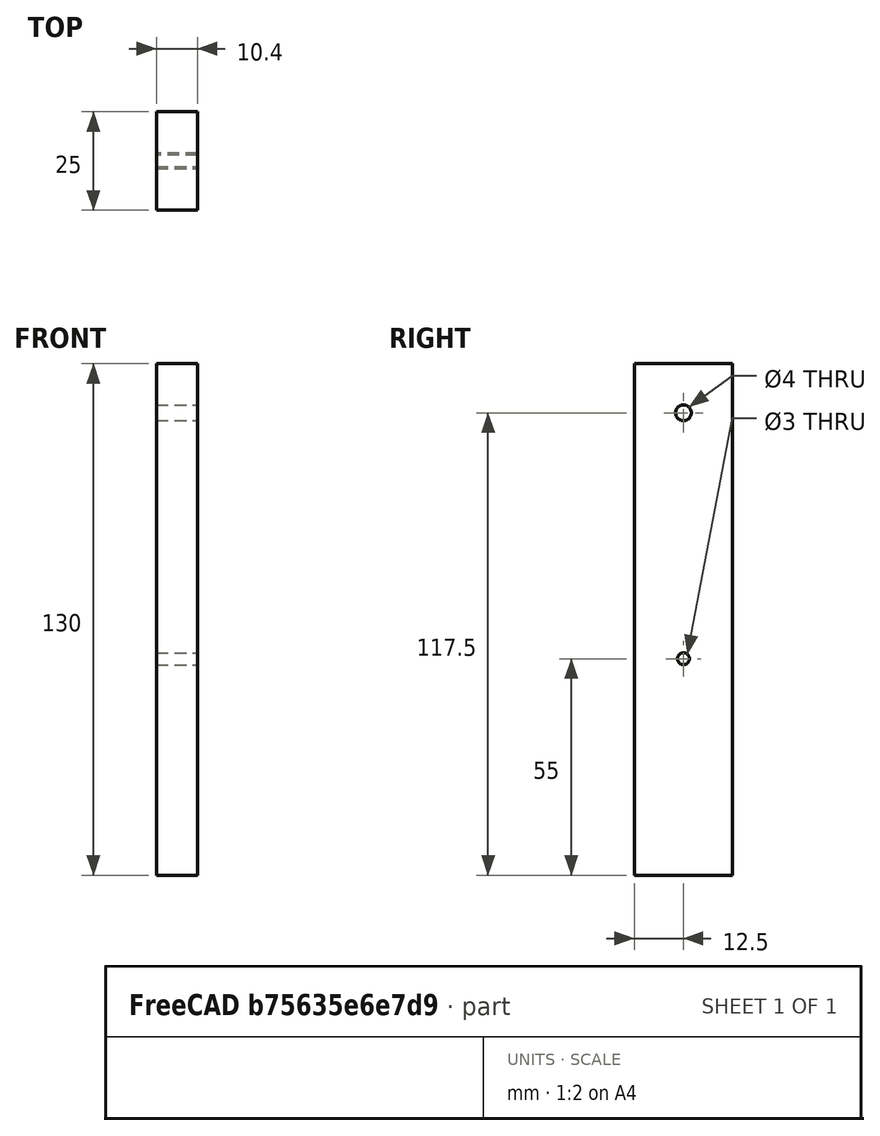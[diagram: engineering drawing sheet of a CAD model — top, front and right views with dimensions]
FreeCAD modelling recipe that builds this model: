
FCSTD DOCUMENT  (FreeCAD 0.19R24267 +99 (Git))
Label: Standbeine
License: All rights reserved
LicenseURL: http://en.wikipedia.org/wiki/All_rights_reserved
objects: TechDraw::DrawViewDimension×6, TechDraw::DrawProjGroupItem×4, TechDraw::DrawProjGroup×4, Sketcher::SketchObject×3, PartDesign::Pocket×2, PartDesign::Pad×1, PartDesign::Body×1, TechDraw::DrawSVGTemplate×1, TechDraw::DrawPage×1
note: 10 computed .brp shape members not serialized (recipe doc carries the construction recipe); baked Part::Feature solids carry a one-line shape summary decoded from their .brp

FEATURE [Sketcher::SketchObject] Sketch
  FullyConstrained = true
  MapMode = 5
  Support = -> [XY_Plane]
  sketch-geometry (4):
    g0: LineSegment StartX=-5.2 StartY=12.5 StartZ=0 EndX=5.2 EndY=12.5 EndZ=0
    g1: LineSegment StartX=5.2 StartY=12.5 StartZ=0 EndX=5.2 EndY=-12.5 EndZ=0
    g2: LineSegment StartX=5.2 StartY=-12.5 StartZ=0 EndX=-5.2 EndY=-12.5 EndZ=0
    g3: LineSegment StartX=-5.2 StartY=-12.5 StartZ=0 EndX=-5.2 EndY=12.5 EndZ=0
  constraints (11):
    c: Coincident(g0,g1)
    c: Coincident(g1,g2)
    c: Coincident(g2,g3)
    c: Coincident(g3,g0)
    c: Horizontal(g0)
    c: Horizontal(g2)
    c: Vertical(g1)
    c: Vertical(g3)
    c: DistanceY(g1,g1) = 25
    c: DistanceX(g0,g0) = 10.4
    c: Symmetric(g0,g1,g-1)
FEATURE [PartDesign::Pad] Pad
  Direction = (1,1,1)
  Length = 130
  Length2 = 100
  Profile = -> Sketch
  Type = 0
FEATURE [Sketcher::SketchObject] Sketch001
  FullyConstrained = true
  MapMode = 5
  Placement = pos=(5.2,0,0) rot=(0.57735,0.57735,0.57735;2.0944rad)
  Support = -> [Pad]
  sketch-geometry (2):
    g0: Circle CenterX=0 CenterY=55 CenterZ=0 NormalX=0 NormalY=0 NormalZ=1 AngleXU=0 Radius=1.5
    g1: GeomPoint X=0 Y=53.5 Z=0
  constraints (6):
    c: PointOnObject(g0,g-2)
    c: DistanceY(g-1,g0) = 55
    c: Diameter(g0) = 3
    c: PointOnObject(g1,g0)
    c: PointOnObject(g1,g-2)
    c: DistanceY(g-1,g1) = 53.5
FEATURE [PartDesign::Pocket] Pocket
  BaseFeature = -> Pad
  Length = 100
  Length2 = 100
  Profile = -> Sketch001
  Type = 0
FEATURE [Sketcher::SketchObject] Sketch002
  ExternalGeometry = -> [Pocket]
  FullyConstrained = true
  MapMode = 5
  Placement = pos=(5.2,0,0) rot=(0.57735,0.57735,0.57735;2.0944rad)
  Support = -> [Pocket]
  sketch-geometry (3):
    g0: Circle CenterX=0 CenterY=117.5 CenterZ=0 NormalX=0 NormalY=0 NormalZ=1 AngleXU=0 Radius=2
    g1: LineSegment StartX=12.5 StartY=130 StartZ=0 EndX=0 EndY=130 EndZ=0
    g2: LineSegment StartX=0 StartY=130 StartZ=0 EndX=0 EndY=117.5 EndZ=0
  constraints (8):
    c: PointOnObject(g0,g-2)
    c: Coincident(g1,g-3)
    c: PointOnObject(g1,g-2)
    c: Horizontal(g1)
    c: Coincident(g2,g1)
    c: Coincident(g2,g0)
    c: Equal(g2,g1)
    c: Diameter(g0) = 4
FEATURE [PartDesign::Pocket] Pocket001
  BaseFeature = -> Pocket
  Length = 100
  Length2 = 100
  Profile = -> Sketch002
  Type = 0
FEATURE [PartDesign::Body] Body
  Group = -> [Sketch,Pad,Sketch001,Pocket,Sketch002,Pocket001]
  Origin = -> Origin
  Tip = -> Pocket001
FEATURE [TechDraw::DrawSVGTemplate] Template
  EditableTexts = APPROVER_NAME=APPROVER NAME; AUTHOR_NAME=AUTHOR NAME; DATE=YYYY-MM-DD; DN=DN; DOCUMENT_TYPE=Mechanical assembly drawing; OWNER_NAME=OWNER NAME; PM=PM; PN=PN; REVISION=REV A; RIGHTS=(R) DO NOT DUPLICATE THIS DRAWING TO THIRD PARTIES WITHOUT OWNER'S PERMISSION !; SCALE=M x:x; SHEET=99 of 99; SIZE=A4; TITLELINE-1=FreeCAD; TOLERANCE=+/- ?
  Height = 210
  Orientation = 1
  Width = 297
FEATURE [TechDraw::DrawProjGroupItem] ProjItem  label="Front"
  Caption = Seitenansicht
  CoarseView = false
  Direction = (1,0,0)
  Focus = 100
  HardHidden = false
  IsoCount = 0
  IsoHidden = false
  IsoVisible = false
  LockPosition = true
  Perspective = false
  Rotation = 0
  RotationVector = (0,1,0)
  ScaleType = 2
  SeamHidden = false
  SeamVisible = true
  SmoothHidden = false
  SmoothVisible = true
  Source = -> [Body]
  Type = 0
  X = 0
  XDirection = (0,1,0)
  Y = 0
FEATURE [TechDraw::DrawProjGroup] ProjGroup
  Anchor = -> ProjItem
  AutoDistribute = true
  LockPosition = false
  ProjectionType = 0
  Rotation = 0
  ScaleType = 0
  Source = -> [Body]
  Views = -> [ProjItem]
  X = 29.568
  Y = 123.01
  spacingX = 15
  spacingY = 15
FEATURE [TechDraw::DrawViewDimension] Dimension
  Arbitrary = false
  ArbitraryTolerances = false
  EqualTolerance = true
  FormatSpec = %.2f
  FormatSpecOverTolerance = %+.2f
  FormatSpecUnderTolerance = %+.2f
  Inverted = false
  LockPosition = false
  MeasureType = 1
  OverTolerance = 0
  References2D = -> [ProjItem]
  Rotation = 0
  ScaleType = 0
  TheoreticalExact = false
  Type = 2
  UnderTolerance = 0
  X = 16.5326
  Y = 0
FEATURE [TechDraw::DrawViewDimension] Dimension001
  Arbitrary = false
  ArbitraryTolerances = false
  EqualTolerance = true
  FormatSpec = %.2f
  FormatSpecOverTolerance = %+.2f
  FormatSpecUnderTolerance = %+.2f
  Inverted = false
  LockPosition = false
  MeasureType = 1
  OverTolerance = 0
  References2D = -> [ProjItem]
  Rotation = 0
  ScaleType = 0
  TheoreticalExact = false
  Type = 1
  UnderTolerance = 0
  X = 1.01942
  Y = 75.8738
FEATURE [TechDraw::DrawViewDimension] Dimension002
  Arbitrary = false
  ArbitraryTolerances = false
  EqualTolerance = true
  FormatSpec = ⌀%.2f
  FormatSpecOverTolerance = %+.2f
  FormatSpecUnderTolerance = %+.2f
  Inverted = false
  LockPosition = false
  MeasureType = 1
  OverTolerance = 0
  References2D = -> [ProjItem]
  Rotation = 0
  ScaleType = 0
  TheoreticalExact = false
  Type = 5
  UnderTolerance = 0
  X = -6.79612
  Y = 62.8641
FEATURE [TechDraw::DrawViewDimension] Dimension003
  Arbitrary = false
  ArbitraryTolerances = false
  EqualTolerance = true
  FormatSpec = ⌀%.2f
  FormatSpecOverTolerance = %+.2f
  FormatSpecUnderTolerance = %+.2f
  Inverted = false
  LockPosition = false
  MeasureType = 1
  OverTolerance = 0
  References2D = -> [ProjItem]
  Rotation = 0
  ScaleType = 0
  TheoreticalExact = false
  Type = 5
  UnderTolerance = 0
  X = -6.45631
  Y = 1.35922
FEATURE [TechDraw::DrawViewDimension] Dimension004
  Arbitrary = false
  ArbitraryTolerances = false
  EqualTolerance = true
  FormatSpec = %.2f
  FormatSpecOverTolerance = %+.2f
  FormatSpecUnderTolerance = %+.2f
  Inverted = false
  LockPosition = false
  MeasureType = 1
  OverTolerance = 0
  References2D = -> [ProjItem]
  Rotation = 0
  ScaleType = 0
  TheoreticalExact = false
  Type = 2
  UnderTolerance = 0
  X = 34.9611
  Y = 46.523
FEATURE [TechDraw::DrawViewDimension] Dimension005
  Arbitrary = false
  ArbitraryTolerances = false
  EqualTolerance = true
  FormatSpec = %.2f
  FormatSpecOverTolerance = %+.2f
  FormatSpecUnderTolerance = %+.2f
  Inverted = false
  LockPosition = false
  MeasureType = 1
  OverTolerance = 0
  References2D = -> [ProjItem]
  Rotation = 0
  ScaleType = 0
  TheoreticalExact = false
  Type = 2
  UnderTolerance = 0
  X = 53.7452
  Y = 31.8083
FEATURE [TechDraw::DrawProjGroupItem] ProjItem001  label="Front001"
  Caption = Frontansicht
  CoarseView = false
  Direction = (0,1,0)
  Focus = 100
  HardHidden = false
  IsoCount = 0
  IsoHidden = false
  IsoVisible = false
  LockPosition = true
  Perspective = false
  Rotation = 0
  RotationVector = (-1,0,0)
  ScaleType = 2
  SeamHidden = false
  SeamVisible = true
  SmoothHidden = false
  SmoothVisible = true
  Source = -> [Body]
  Type = 0
  X = 0
  XDirection = (-1,0,0)
  Y = 0
FEATURE [TechDraw::DrawProjGroup] ProjGroup001
  Anchor = -> ProjItem001
  AutoDistribute = true
  LockPosition = false
  ProjectionType = 0
  Rotation = 0
  ScaleType = 0
  Source = -> [Body]
  Views = -> [ProjItem001]
  X = 130.198
  Y = 118.339
  spacingX = 15
  spacingY = 15
FEATURE [TechDraw::DrawProjGroupItem] ProjItem002  label="Front002"
  Caption = Draufsicht
  CoarseView = false
  Direction = (0,0,1)
  Focus = 100
  HardHidden = false
  IsoCount = 0
  IsoHidden = false
  IsoVisible = false
  LockPosition = true
  Perspective = false
  Rotation = 0
  RotationVector = (-1,0,0)
  ScaleType = 2
  SeamHidden = false
  SeamVisible = true
  SmoothHidden = false
  SmoothVisible = true
  Source = -> [Body]
  Type = 0
  X = 0
  XDirection = (-1,0,0)
  Y = 0
FEATURE [TechDraw::DrawProjGroup] ProjGroup002
  Anchor = -> ProjItem002
  AutoDistribute = true
  LockPosition = false
  ProjectionType = 0
  Rotation = 0
  ScaleType = 0
  Source = -> [Body]
  Views = -> [ProjItem002]
  X = 173.006
  Y = 170.762
  spacingX = 15
  spacingY = 15
FEATURE [TechDraw::DrawProjGroupItem] ProjItem003  label="Front003"
  Caption = Schrägsicht
  CoarseView = false
  Direction = (0.5,0.5,0.707)
  Focus = 100
  HardHidden = false
  IsoCount = 0
  IsoHidden = false
  IsoVisible = false
  LockPosition = true
  Perspective = false
  Rotation = 0
  RotationVector = (-0.707,0.707,0)
  ScaleType = 2
  SeamHidden = false
  SeamVisible = true
  SmoothHidden = false
  SmoothVisible = true
  Source = -> [Body]
  Type = 0
  X = 0
  XDirection = (-0.707,0.707,0)
  Y = 0
FEATURE [TechDraw::DrawProjGroup] ProjGroup003
  Anchor = -> ProjItem003
  AutoDistribute = true
  LockPosition = false
  ProjectionType = 0
  Rotation = 0
  ScaleType = 0
  Source = -> [Body]
  Views = -> [ProjItem003]
  X = 226.67
  Y = 120.82
  spacingX = 15
  spacingY = 15
FEATURE [TechDraw::DrawPage] Page
  KeepUpdated = true
  NextBalloonIndex = 1
  ProjectionType = 0
  Template = -> Template
  Views = -> [ProjGroup,Dimension,Dimension001,Dimension002,Dimension003,Dimension004,Dimension005,ProjGroup001,ProjGroup002,ProjGroup003]
